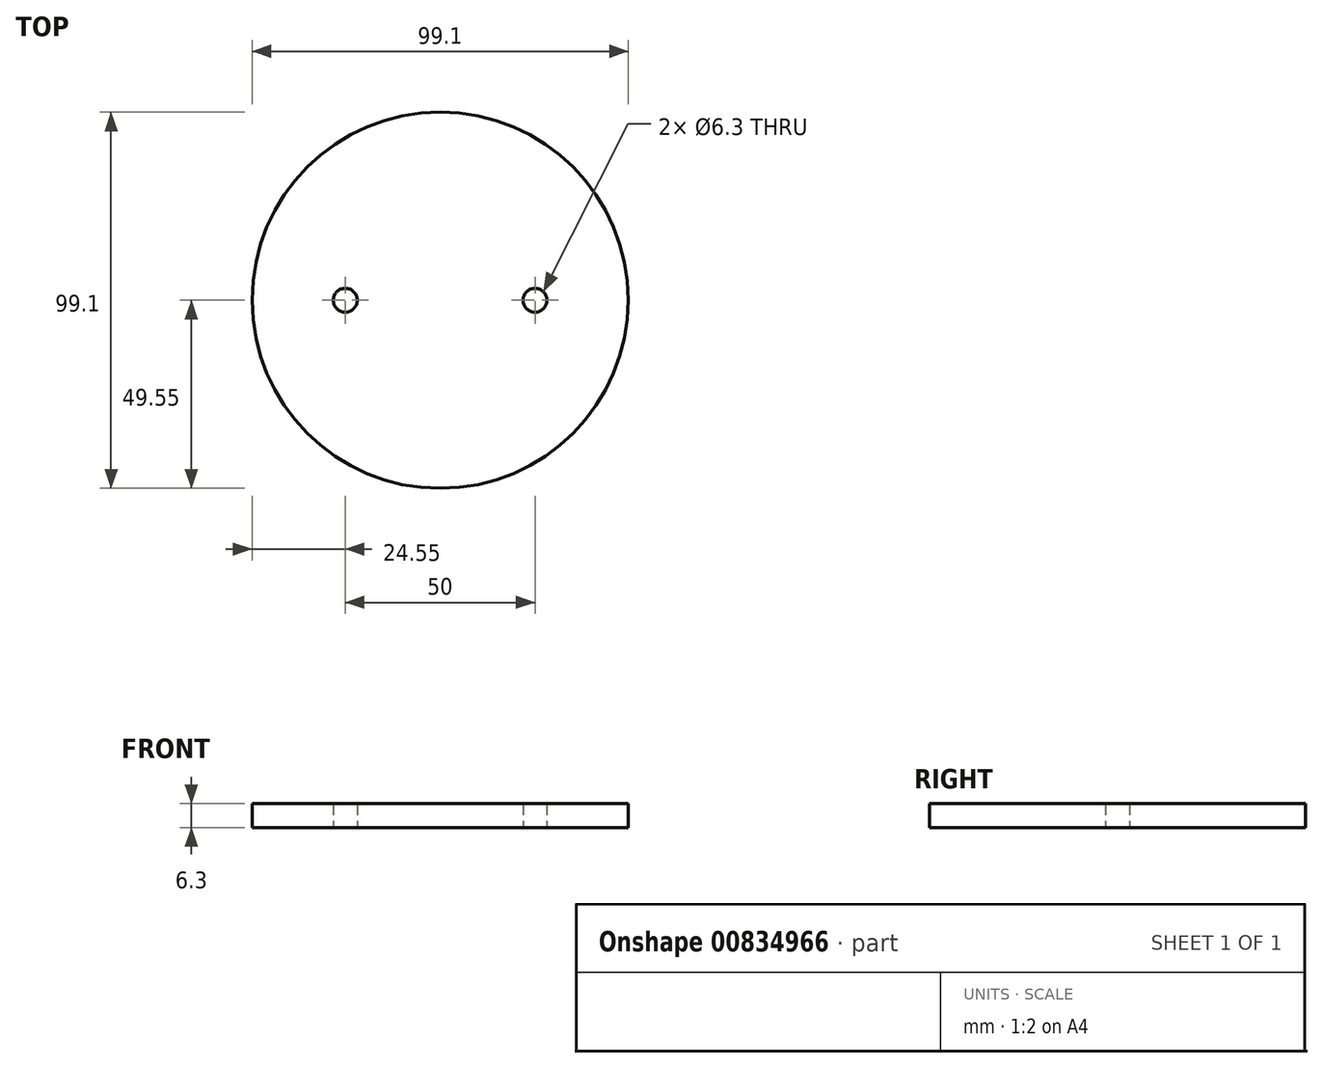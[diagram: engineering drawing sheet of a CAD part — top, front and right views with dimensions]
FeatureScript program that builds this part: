
annotation { "Feature Type Name" : "Feature", "Feature Type Description" : "" }
export const myFeature = defineFeature(function(context is Context, id is Id, definition is map)
    precondition{}
    {
        {
            var Q0;
            Q0=qCreatedBy(makeId("Front.planeOp"),FACE);
            var sketch = newSketch(context, id + "F0", { "sketchPlane" : qUnion([Q0])});
            skLineSegment(sketch, "E0", {"start": v(-49.55, 6.3) * mm, "end": v(-49.55, 12.6) * mm});
            skLineSegment(sketch, "E1", {"start": v(-49.55, 12.6) * mm, "end": v(0, 12.6) * mm});
            skLineSegment(sketch, "E2", {"start": v(0, 12.6) * mm, "end": v(0, 0) * mm});
            skLineSegment(sketch, "E3", {"start": v(0, 2.5) * mm, "end": v(0, -12.8) * mm});
            skLineSegment(sketch, "E4", {"start": v(-49.55, 6.3) * mm, "end": v(0, 6.3) * mm});
            skLineSegment(sketch, "E5", {"start": v(0, 6.3) * mm, "end": v(0, 12.6) * mm});
            skSolve(sketch);
        }
        {
            var Q0;
            Q0=makeQuery(id+"F0.imprint","IMPRINT",FACE,{"disambiguationData":[TD([[makeQuery(id+"F0.imprint","IMPRINT",EDGE,{"derivedFrom":sQuery(id+"F0.wireOp",EDGE,"KPOy5Dg6-L2cZ-RmG1-JL2Y-emlwueLXsoj0")}),-1.0]])]});
            var Q1;
            Q1=makeQuery(id+"F0.imprint","IMPRINT",FACE,{"disambiguationData":[TD([[makeQuery(id+"F0.imprint","IMPRINT",EDGE,{"derivedFrom":sQuery(id+"F0.wireOp",EDGE,"E0")}),-1.0]])]});
            var Q2;
            Q2=sQuery(id+"F0.wireOp",EDGE,"E3");
            revolve(context, id + "F1", {"surfaceOperationType" : NewSurfaceOperationType.NEW, "entities" : qUnion([Q0, Q1]), "axis" : qUnion([Q2]), "revolveType" : RevolveType.FULL});
        }
        {
            var Q0;
            Q0=qCreatedBy(makeId("Top.planeOp"),FACE);
            var sketch = newSketch(context, id + "F2", { "sketchPlane" : qUnion([Q0])});
            skPoint(sketch, "E6", {"position": v(25, 0) * mm});
            skPoint(sketch, "E7", {"position": v(-25, 0) * mm});
            skSolve(sketch);
        }
        {
            var Q0;
            Q0=sQuery(id+"F2.wireOp",VERTEX,"E6");
            var Q1;
            Q1=sQuery(id+"F2.wireOp",VERTEX,"E7");
            var Q2;
            Q2=makeQuery(id+"F1.opRevolve","SWEPT_BODY",BODY,{"disambiguationData":[OSD([sQuery(id+"F0.wireOp",EDGE,"KPOy5Dg6-L2cZ-RmG1-JL2Y-emlwueLXsoj0"),sQuery(id+"F0.wireOp",EDGE,"zHhjstx2-zBRU-L1TK-amxH-6YpQQBydax53"),sQuery(id+"F0.wireOp",EDGE,"E0"),sQuery(id+"F0.wireOp",EDGE,"E1"),sQuery(id+"F0.wireOp",EDGE,"E2"),sQuery(id+"F0.wireOp",EDGE,"xgb0HH9I-2Ncw-98Sp-GOMs-A0hfZGj3ipNI")])]});
            hole(context, id + "F3", {"style" : HoleStyle.SIMPLE, "endStyle" : HoleEndStyle.THROUGH, "oppositeDirection" : true, "holeDiameter" : 6.3 * mm, "majorDiameter" : 5 * mm, "isTappedThrough" : true, "tappedDepth" : 12 * mm, "tapClearance" : 3, "startFromSketch" : true, "locations" : qUnion([Q0, Q1]), "scope" : qUnion([Q2])});
        }
    });
